# Revit family: Platek_Flamingo_Applique
name_source: partatom
category: Apparecchi per illuminazione
revit_build: Autodesk Revit 2017 (Build: 20160225_1515(x64)
units: mm (PartAtom-declared; Revit-internal decimal feet)

## family parameters
Basato su piano di lavoro = No
Condiviso = No
Punto di calcolo locali = No
Quota connettore circolare = Usa diametro
Sempre verticale = Sì
Sorgente d'illuminazione = Sì
Taglio con vuoti quando caricato = No
Tipo di parte = Normale

## types (1)
- 3010116_9W_LED_3000K
    Angolo inclinazione = 90.00°
    Beam Angle = 76.00°
    Body = PLK_Black
    CRI = >80
    Cable Lenght = 0,15 (2x1 mm²)
    Carico apparente = 0 VA
    Codice assieme = 3010116.01(Black); 3010116.09(Bronze)
    Colour Temperature = 3000 K
    Commenti sul tipo = Facades
    Descrizione = Outdoor Lighting, Wall mounted
    Diffuse Type = Polycarbonate
    Dimmable = No
    Emetti da diametro cerchio = 50 mm  [stored 0.164042 ft]
    Energy Efficiency Rating = A/A+/A++
    File diagramma fotometrico = 3010116.IES
    Filtro dei colori = 16777215
    Frequency = 50/60 Hz
    IK Rating = IK 06
    IP Rating = IP65
    Immagine tipo = flamingo_applique.jpg
    Insulation Class = 1
    LED Protection = Surge protection included
    Lampada = LED
    Light Source = PLK_Light Source
    Luminaire Luminous Flux = 385 lm
    Luminaire Luminous Intensity = 259 cd
    Luminaire Wattage = 9 W
    Manufacturer Comment = IP68 connector included
    Modello = Flamingo Applique
    Mounting Type = Wall
    Nota chiave = Other LED colors available on request
    PLATEK Article Code = 3010116
    Power Supply Unit = Included
    Product Dimension = L370mmxH225mm
    Product Documentation Link = http://www.platek.eu
    Product Page URL = http://www.platek.eu
    Produttore = PLATEK SRL
    Rendi la forma visibile nel rendering = No
    Supply Voltage = 230 V
    Supply Voltage Max = 240 V
    Supply Voltage Min = 220 V
    URL = www.platek.eu
    Variazione temperatura colore lampada con luminosità attenuata = <Nessuno>

note: [stored X ft] marks values corroborated as IEEE doubles in the binary element streams (Revit-internal decimal feet)
